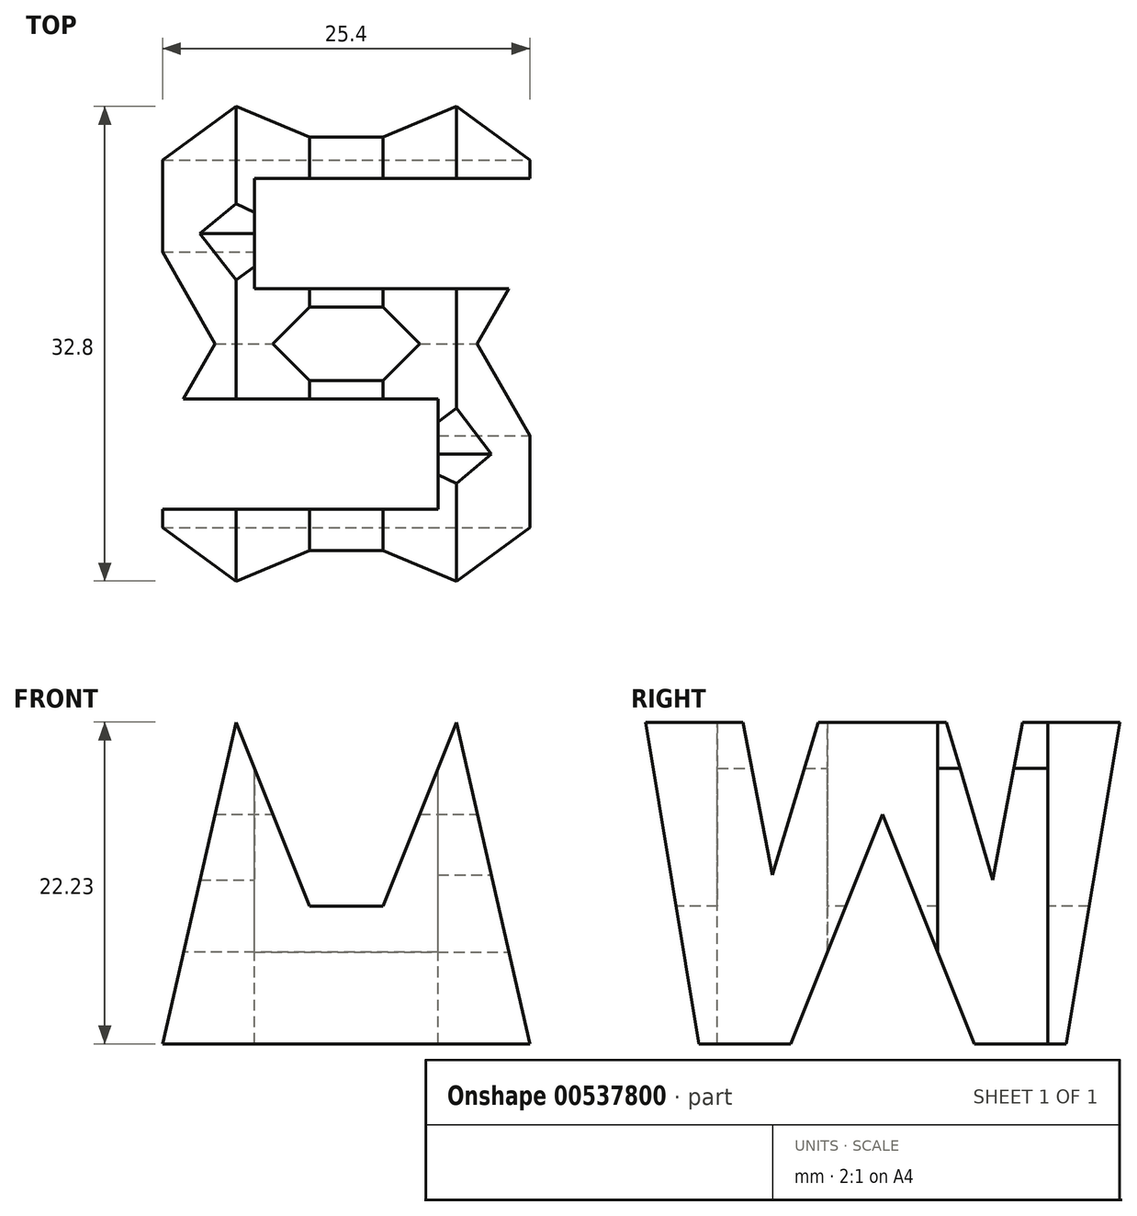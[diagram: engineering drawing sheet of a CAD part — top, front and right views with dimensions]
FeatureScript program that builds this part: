
annotation { "Feature Type Name" : "Feature", "Feature Type Description" : "" }
export const myFeature = defineFeature(function(context is Context, id is Id, definition is map)
    precondition{}
    {
        {
            var Q0;
            Q0=qCreatedBy(makeId("Front.planeOp"),FACE);
            var sketch = newSketch(context, id + "F0", { "sketchPlane" : qUnion([Q0])});
            skLineSegment(sketch, "E0", {"start": v(0, 0) * mm, "end": v(0, 38.1) * mm});
            skLineSegment(sketch, "E1", {"start": v(0, 38.1) * mm, "end": v(38.1, 38.1) * mm});
            skLineSegment(sketch, "E2", {"start": v(38.1, 0) * mm, "end": v(38.1, 38.1) * mm});
            skLineSegment(sketch, "E3", {"start": v(0, 0) * mm, "end": v(38.1, 0) * mm});
            skSolve(sketch);
        }
        {
            var Q0;
            Q0 = qSketchRegion(id + "F0", true);
            extrude(context, id + "F1", {"entities" : qUnion([Q0]), "depth" : 38.1 * mm, "offsetDistance" : 25.4 * mm});
        }
        {
            var Q0;
            Q0=qCreatedBy(makeId("Front.planeOp"),FACE);
            cPlane(context, id + "F2", {"entities" : qUnion([Q0]), "cplaneType" : CPlaneType.OFFSET, "offset" : 38.1 * mm, "width" : 152.4 * mm, "height" : 152.4 * mm});
        }
        {
            var Q0;
            Q0=qCreatedBy(makeId("Right.planeOp"),FACE);
            cPlane(context, id + "F3", {"entities" : qUnion([Q0]), "cplaneType" : CPlaneType.OFFSET, "offset" : 38.1 * mm, "width" : 152.4 * mm, "height" : 152.4 * mm});
        }
        {
            var Q0;
            Q0=qCreatedBy(makeId("Top.planeOp"),FACE);
            cPlane(context, id + "F4", {"entities" : qUnion([Q0]), "cplaneType" : CPlaneType.OFFSET, "offset" : 38.1 * mm, "width" : 152.4 * mm, "height" : 152.4 * mm});
        }
        {
            var Q0;
            Q0=qCreatedBy(id+"F3.planeOp",FACE);
            var sketch = newSketch(context, id + "F5", { "sketchPlane" : qUnion([Q0])});
            skLineSegment(sketch, "E4", {"start": v(0, 0) * mm, "end": v(0, 38.1) * mm});
            skLineSegment(sketch, "E5", {"start": v(0, 38.1) * mm, "end": v(-38.1, 38.1) * mm});
            skLineSegment(sketch, "E6", {"start": v(-38.1, 38.1) * mm, "end": v(-38.1, 0) * mm});
            skLineSegment(sketch, "E7", {"start": v(-38.1, 0) * mm, "end": v(0, 0) * mm});
            skLineSegment(sketch, "E8", {"start": v(-38.1, 38.1) * mm, "end": v(-31.75, 0) * mm});
            skPoint(sketch, "E9.endSnap0", {"position": v(-19.05, 0) * mm});
            skLineSegment(sketch, "E10", {"start": v(-6.35, 0) * mm, "end": v(0, 38.1) * mm});
            skLineSegment(sketch, "E11", {"start": v(-31.75, 38.1) * mm, "end": v(-26.67, 11.67) * mm});
            skLineSegment(sketch, "E12", {"start": v(-11.43, 11.32) * mm, "end": v(-6.35, 38.1) * mm});
            skLineSegment(sketch, "E13", {"start": v(-26.67, 11.67) * mm, "end": v(-21.59, 28.58) * mm});
            skLineSegment(sketch, "E14", {"start": v(-21.59, 28.58) * mm, "end": v(-16.51, 28.58) * mm});
            skLineSegment(sketch, "E15", {"start": v(-31.75, 0) * mm, "end": v(-25.4, 0) * mm});
            skLineSegment(sketch, "E16", {"start": v(-25.4, 0) * mm, "end": v(-19.05, 15.88) * mm});
            skLineSegment(sketch, "E17", {"start": v(-6.35, 0) * mm, "end": v(-12.7, 0) * mm});
            skLineSegment(sketch, "E18", {"start": v(-12.7, 0) * mm, "end": v(-19.05, 15.88) * mm});
            skLineSegment(sketch, "E19", {"start": v(-16.51, 28.58) * mm, "end": v(-11.43, 11.32) * mm});
            skSolve(sketch);
        }
        {
            var Q0;
            {var subQ1=sQuery(id+"F5.wireOp",EDGE,"E11");Q0=makeQuery(id+"F5.imprint","IMPRINT",FACE,{"disambiguationData":[TD([[makeQuery(id+"F5.imprint","IMPRINT",EDGE,{"derivedFrom":subQ1}),1.0]])]});}
            var Q1;
            {var subQ0=sQuery(id+"F5.wireOp",EDGE,"E6");Q1=makeQuery(id+"F5.imprint","IMPRINT",FACE,{"disambiguationData":[TD([[makeQuery(id+"F5.imprint","IMPRINT",EDGE,{"derivedFrom":subQ0}),1.0]])]});}
            var Q2;
            {var subQ0=sQuery(id+"F5.wireOp",EDGE,"E16");Q2=makeQuery(id+"F5.imprint","IMPRINT",FACE,{"disambiguationData":[TD([[makeQuery(id+"F5.imprint","IMPRINT",EDGE,{"derivedFrom":subQ0}),-1.0]])]});}
            var Q3;
            {var subQ0=sQuery(id+"F5.wireOp",EDGE,"E4");Q3=makeQuery(id+"F5.imprint","IMPRINT",FACE,{"disambiguationData":[TD([[makeQuery(id+"F5.imprint","IMPRINT",EDGE,{"derivedFrom":subQ0}),1.0]])]});}
            extrude(context, id + "F6", {"entities" : qUnion([Q0, Q1, Q2, Q3]), "operationType" : NewBodyOperationType.REMOVE, "oppositeDirection" : true, "depth" : 50.8 * mm, "offsetDistance" : 25.4 * mm});
        }
        {
            var Q0;
            Q0=qCreatedBy(id+"F2.planeOp",FACE);
            var sketch = newSketch(context, id + "F7", { "sketchPlane" : qUnion([Q0])});
            skLineSegment(sketch, "E20", {"start": v(0, 0) * mm, "end": v(0, 38.1) * mm});
            skLineSegment(sketch, "E21", {"start": v(0, 38.1) * mm, "end": v(38.1, 38.1) * mm});
            skLineSegment(sketch, "E22", {"start": v(38.1, 38.1) * mm, "end": v(38.1, 0) * mm});
            skLineSegment(sketch, "E23", {"start": v(38.1, 0) * mm, "end": v(0, 0) * mm});
            skLineSegment(sketch, "E24", {"start": v(0, 0) * mm, "end": v(6.35, 38.1) * mm});
            skLineSegment(sketch, "E25", {"start": v(6.35, 38.1) * mm, "end": v(12.7, 38.1) * mm});
            skLineSegment(sketch, "E26", {"start": v(25.4, 38.1) * mm, "end": v(31.75, 38.1) * mm});
            skLineSegment(sketch, "E27", {"start": v(31.75, 38.1) * mm, "end": v(38.1, 0) * mm});
            skLineSegment(sketch, "E28", {"start": v(6.35, 0) * mm, "end": v(0, 0) * mm});
            skLineSegment(sketch, "E29", {"start": v(38.1, 0) * mm, "end": v(31.75, 0) * mm});
            skLineSegment(sketch, "E30", {"start": v(12.7, 38.1) * mm, "end": v(19.05, 22.22) * mm});
            skLineSegment(sketch, "E31", {"start": v(19.05, 22.22) * mm, "end": v(25.4, 38.1) * mm});
            skLineSegment(sketch, "E32", {"start": v(6.35, 0) * mm, "end": v(11.43, 22.23) * mm});
            skLineSegment(sketch, "E33", {"start": v(11.43, 22.23) * mm, "end": v(16.51, 9.52) * mm});
            skLineSegment(sketch, "E34", {"start": v(26.67, 22.23) * mm, "end": v(31.75, 0) * mm});
            skLineSegment(sketch, "E35", {"start": v(16.51, 9.52) * mm, "end": v(21.59, 9.52) * mm});
            skLineSegment(sketch, "E36", {"start": v(21.59, 9.52) * mm, "end": v(26.67, 22.23) * mm});
            skSolve(sketch);
        }
        {
            var Q0;
            {var subQ0=sQuery(id+"F7.wireOp",EDGE,"E20");Q0=makeQuery(id+"F7.imprint","IMPRINT",FACE,{"disambiguationData":[TD([[makeQuery(id+"F7.imprint","IMPRINT",EDGE,{"derivedFrom":subQ0}),-1.0]])]});}
            var Q1;
            {var subQ0=sQuery(id+"F7.wireOp",EDGE,"E30");Q1=makeQuery(id+"F7.imprint","IMPRINT",FACE,{"disambiguationData":[TD([[makeQuery(id+"F7.imprint","IMPRINT",EDGE,{"derivedFrom":subQ0}),1.0]])]});}
            var Q2;
            {var subQ0=sQuery(id+"F7.wireOp",EDGE,"E22");Q2=makeQuery(id+"F7.imprint","IMPRINT",FACE,{"disambiguationData":[TD([[makeQuery(id+"F7.imprint","IMPRINT",EDGE,{"derivedFrom":subQ0}),-1.0]])]});}
            var Q3;
            Q3=makeQuery(id+"F7.imprint","IMPRINT",FACE,{"disambiguationData":[TD([[makeQuery(id+"F7.imprint","IMPRINT",EDGE,{"derivedFrom":sQuery(id+"F7.wireOp",EDGE,"E23")}),-1.0]])]});
            extrude(context, id + "F8", {"entities" : qUnion([Q0, Q1, Q2, Q3]), "operationType" : NewBodyOperationType.REMOVE, "oppositeDirection" : true, "depth" : 38.1 * mm, "offsetDistance" : 25.4 * mm});
        }
        {
            var Q0;
            Q0=qCreatedBy(id+"F4.planeOp",FACE);
            var sketch = newSketch(context, id + "F9", { "sketchPlane" : qUnion([Q0])});
            skLineSegment(sketch, "E37", {"start": v(51.78, -7.62) * mm, "end": v(12.7, -7.62) * mm});
            skLineSegment(sketch, "E38", {"start": v(12.7, -7.62) * mm, "end": v(12.7, -15.24) * mm});
            skLineSegment(sketch, "E39", {"start": v(12.7, -15.24) * mm, "end": v(51.97, -15.24) * mm});
            skLineSegment(sketch, "E40", {"start": v(0, -22.86) * mm, "end": v(25.4, -22.86) * mm});
            skLineSegment(sketch, "E41", {"start": v(25.4, -22.86) * mm, "end": v(25.4, -30.48) * mm});
            skLineSegment(sketch, "E42", {"start": v(25.4, -30.48) * mm, "end": v(0, -30.48) * mm});
            skLineSegment(sketch, "E43", {"start": v(0, -30.48) * mm, "end": v(0, -22.86) * mm});
            skLineSegment(sketch, "E44", {"start": v(51.78, -7.62) * mm, "end": v(51.97, -15.24) * mm});
            skLineSegment(sketch, "E45", {"start": v(0, 0) * mm, "end": v(0, -38.1) * mm});
            skLineSegment(sketch, "E46", {"start": v(0, -38.1) * mm, "end": v(38.1, -38.1) * mm});
            skLineSegment(sketch, "E47", {"start": v(38.1, -38.1) * mm, "end": v(38.1, 0) * mm});
            skLineSegment(sketch, "E48", {"start": v(38.1, 0) * mm, "end": v(0, 0) * mm});
            skSolve(sketch);
        }
        {
            var Q0;
            {var subQ0=sQuery(id+"F9.wireOp",EDGE,"E40");Q0=makeQuery(id+"F9.imprint","IMPRINT",FACE,{"disambiguationData":[TD([[makeQuery(id+"F9.imprint","IMPRINT",EDGE,{"derivedFrom":subQ0}),-1.0]])]});}
            var Q1;
            {var subQ0=sQuery(id+"F9.wireOp",EDGE,"E38");Q1=makeQuery(id+"F9.imprint","IMPRINT",FACE,{"disambiguationData":[TD([[makeQuery(id+"F9.imprint","IMPRINT",EDGE,{"derivedFrom":subQ0}),1.0]])]});}
            extrude(context, id + "F10", {"entities" : qUnion([Q0, Q1]), "operationType" : NewBodyOperationType.REMOVE, "oppositeDirection" : true, "depth" : 38.1 * mm, "offsetDistance" : 25.4 * mm});
        }
    });
